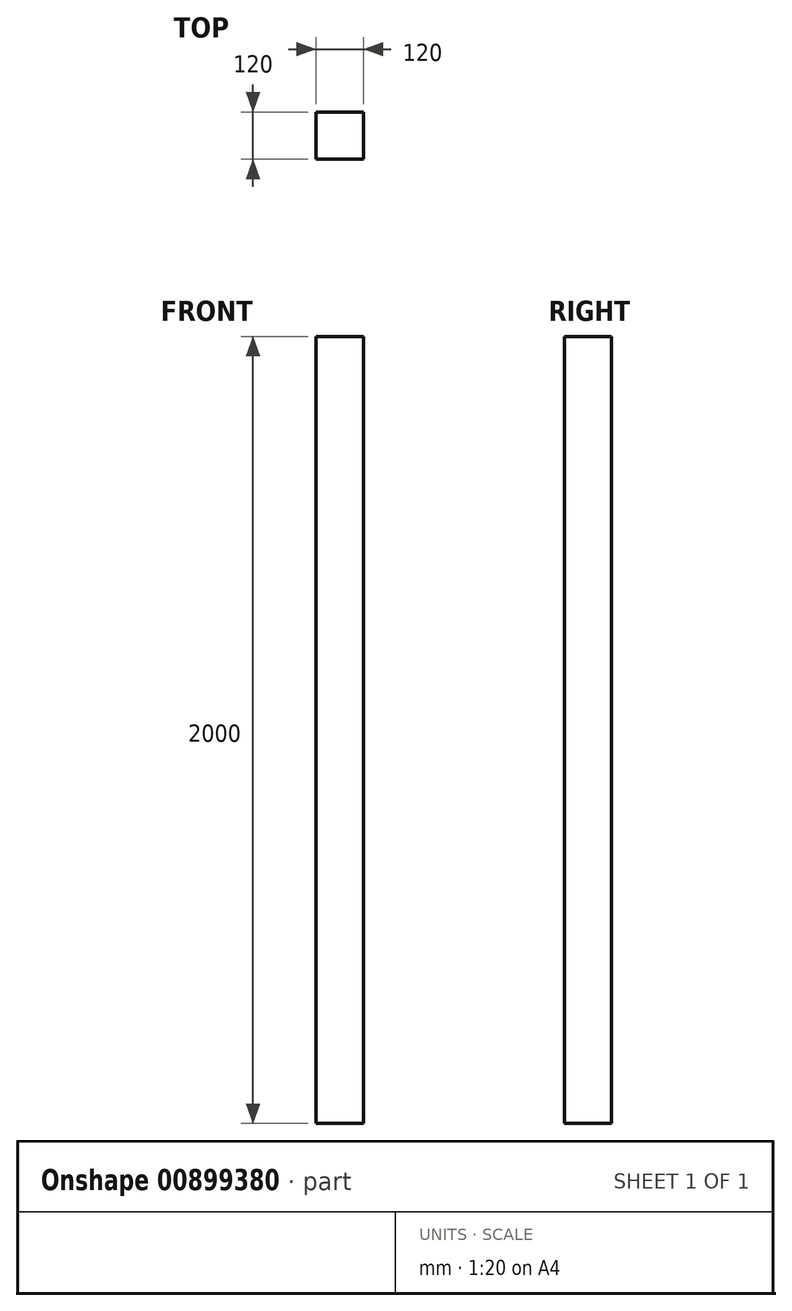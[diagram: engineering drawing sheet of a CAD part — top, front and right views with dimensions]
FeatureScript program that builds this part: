
annotation { "Feature Type Name" : "Feature", "Feature Type Description" : "" }
export const myFeature = defineFeature(function(context is Context, id is Id, definition is map)
    precondition{}
    {
        {
            var Q0;
            Q0=qCreatedBy(makeId("Right.planeOp"),FACE);
            var sketch = newSketch(context, id + "F0", { "sketchPlane" : qUnion([Q0])});
            skLineSegment(sketch, "E0.bottom", {"start": v(-60, 2000) * mm, "end": v(60, 2000) * mm});
            skLineSegment(sketch, "E0.top", {"start": v(-60, 0) * mm, "end": v(60, 0) * mm});
            skLineSegment(sketch, "E0.left", {"start": v(-60, 2000) * mm, "end": v(-60, 0) * mm});
            skLineSegment(sketch, "E0.right", {"start": v(60, 2000) * mm, "end": v(60, 0) * mm});
            skSolve(sketch);
        }
        {
            var Q0;
            Q0=makeQuery(id+"F0.imprint","IMPRINT",FACE,{"disambiguationData":[TD([[makeQuery(id+"F0.imprint","IMPRINT",EDGE,{"derivedFrom":sQuery(id+"F0.wireOp",EDGE,"E0.bottom")}),-1.0]])]});
            extrude(context, id + "F1", {"entities" : qUnion([Q0]), "endBound" : BoundingType.SYMMETRIC, "depth" : 120 * mm, "offsetDistance" : 25 * mm});
        }
    });
